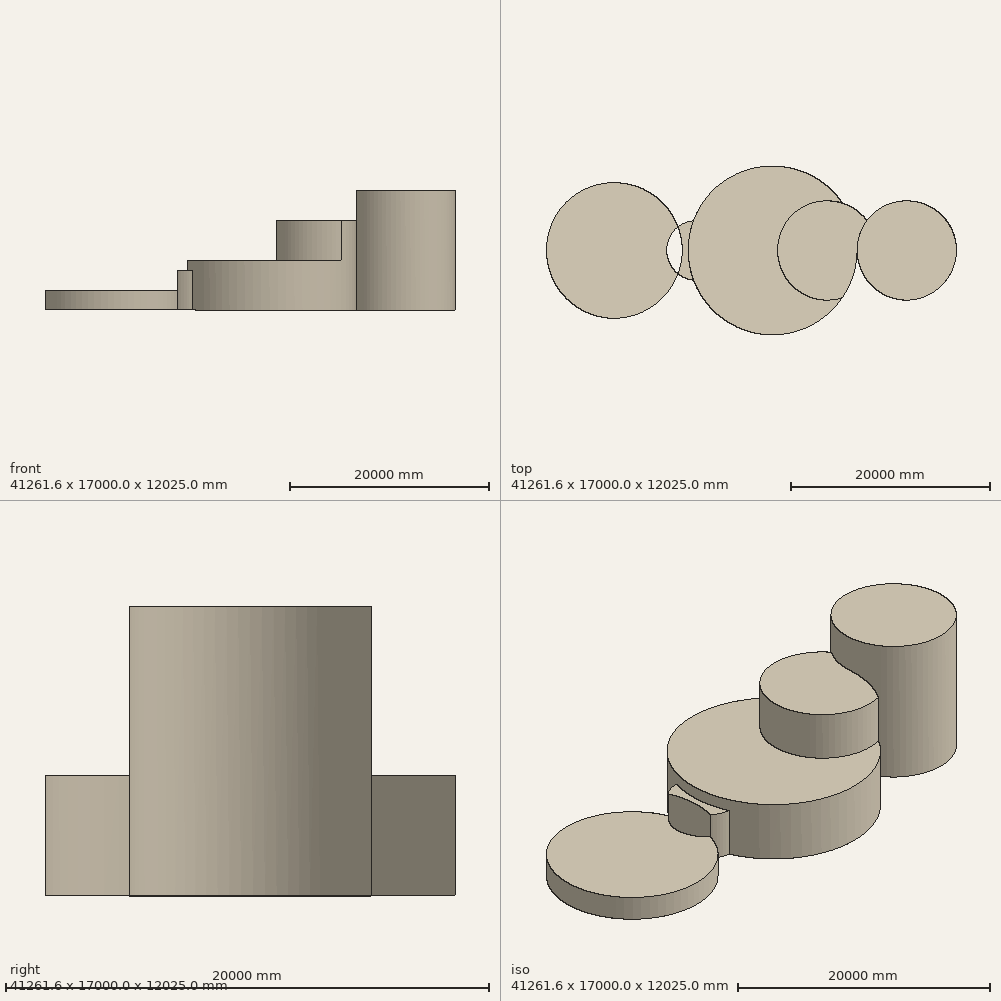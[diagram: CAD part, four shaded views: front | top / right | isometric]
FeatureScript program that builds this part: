
annotation { "Feature Type Name" : "Feature", "Feature Type Description" : "" }
export const myFeature = defineFeature(function(context is Context, id is Id, definition is map)
    precondition{}
    {
        {
            var Q0;
            Q0=qCreatedBy(makeId("Top.planeOp"),FACE);
            var sketch = newSketch(context, id + "F0", { "sketchPlane" : qUnion([Q0])});
            skCircle(sketch, "E0", {"center": v(0, 0) * mm, "radius": 5000 * mm});
            skCircle(sketch, "E1", {"center": v(-8000, 0) * mm, "radius": 5000 * mm});
            skCircle(sketch, "E2", {"center": v(-13500, 0) * mm, "radius": 8500 * mm});
            skCircle(sketch, "E3", {"center": v(-21161.23, 0) * mm, "radius": 3000 * mm});
            skCircle(sketch, "E4", {"center": v(-29430.74, 0) * mm, "radius": 6830.87 * mm});
            skSolve(sketch);
        }
        {
            var Q0;
            {var subQ0=sQuery(id+"F0.wireOp",EDGE,"E1");var subQ1=sQuery(id+"F0.wireOp",EDGE,"E0");var subQ2=makeQuery(id+"F0.imprint","INTERSECT",VERTEX,{"disambiguationData":[OD(0.0)],"derivedFrom":[subQ1,subQ0]});Q0=makeQuery(id+"F0.imprint","IMPRINT",FACE,{"disambiguationData":[TD([[makeQuery(id+"F0.imprint","IMPRINT",EDGE,{"disambiguationData":[TD([[subQ2,1.0]])],"derivedFrom":subQ1}),1.0]])]});}
            var Q1;
            {var subQ0=sQuery(id+"F0.wireOp",EDGE,"E1");var subQ1=sQuery(id+"F0.wireOp",EDGE,"E0");var subQ2=makeQuery(id+"F0.imprint","INTERSECT",VERTEX,{"disambiguationData":[OD(0.0)],"derivedFrom":[subQ1,subQ0]});Q1=makeQuery(id+"F0.imprint","IMPRINT",FACE,{"disambiguationData":[TD([[makeQuery(id+"F0.imprint","IMPRINT",EDGE,{"disambiguationData":[TD([[subQ2,-1.0]])],"derivedFrom":subQ1}),1.0]])]});}
            extrude(context, id + "F1", {"entities" : qUnion([Q0, Q1]), "depth" : 12000 * mm, "offsetDistance" : 25 * mm});
        }
        {
            var Q0;
            {var subQ0=sQuery(id+"F0.wireOp",EDGE,"E1");var subQ1=sQuery(id+"F0.wireOp",EDGE,"E0");var subQ2=makeQuery(id+"F0.imprint","INTERSECT",VERTEX,{"disambiguationData":[OD(0.0)],"derivedFrom":[subQ1,subQ0]});Q0=makeQuery(id+"F0.imprint","IMPRINT",FACE,{"disambiguationData":[TD([[makeQuery(id+"F0.imprint","IMPRINT",EDGE,{"disambiguationData":[TD([[subQ2,-1.0]])],"derivedFrom":subQ1}),-1.0]])]});}
            var Q1;
            {var subQ0=sQuery(id+"F0.wireOp",EDGE,"E2");var subQ1=sQuery(id+"F0.wireOp",EDGE,"E1");var subQ2=makeQuery(id+"F0.imprint","INTERSECT",VERTEX,{"disambiguationData":[OD(0.0)],"derivedFrom":[subQ1,subQ0]});Q1=makeQuery(id+"F0.imprint","IMPRINT",FACE,{"disambiguationData":[TD([[makeQuery(id+"F0.imprint","IMPRINT",EDGE,{"disambiguationData":[TD([[subQ2,-1.0]])],"derivedFrom":subQ1}),1.0]])]});}
            extrude(context, id + "F2", {"entities" : qUnion([Q0, Q1]), "operationType" : NewBodyOperationType.ADD, "depth" : 9000 * mm, "offsetDistance" : 25 * mm, "hasSecondDirection" : true, "secondDirectionOppositeDirection" : true, "secondDirectionDepth" : 25 * mm});
        }
        {
            var Q0;
            {var subQ0=sQuery(id+"F0.wireOp",EDGE,"E4");var subQ1=sQuery(id+"F0.wireOp",EDGE,"E2");var subQ2=makeQuery(id+"F0.imprint","INTERSECT",VERTEX,{"disambiguationData":[OD(0.0)],"derivedFrom":[subQ1,subQ0]});Q0=makeQuery(id+"F0.imprint","IMPRINT",FACE,{"disambiguationData":[TD([[makeQuery(id+"F0.imprint","IMPRINT",EDGE,{"disambiguationData":[TD([[subQ2,-1.0]])],"derivedFrom":subQ1}),1.0]])]});}
            var Q1;
            {var subQ0=sQuery(id+"F0.wireOp",EDGE,"E3");var subQ1=sQuery(id+"F0.wireOp",EDGE,"E2");var subQ2=makeQuery(id+"F0.imprint","INTERSECT",VERTEX,{"disambiguationData":[OD(0.0)],"derivedFrom":[subQ1,subQ0]});Q1=makeQuery(id+"F0.imprint","IMPRINT",FACE,{"disambiguationData":[TD([[makeQuery(id+"F0.imprint","IMPRINT",EDGE,{"disambiguationData":[TD([[subQ2,-1.0]])],"derivedFrom":subQ1}),1.0]])]});}
            var Q2;
            {var subQ0=sQuery(id+"F0.wireOp",EDGE,"E2");var subQ1=sQuery(id+"F0.wireOp",EDGE,"E1");var subQ2=makeQuery(id+"F0.imprint","INTERSECT",VERTEX,{"disambiguationData":[OD(0.0)],"derivedFrom":[subQ1,subQ0]});Q2=makeQuery(id+"F0.imprint","IMPRINT",FACE,{"disambiguationData":[TD([[makeQuery(id+"F0.imprint","IMPRINT",EDGE,{"disambiguationData":[TD([[subQ2,-1.0]])],"derivedFrom":subQ1}),-1.0]])]});}
            extrude(context, id + "F3", {"entities" : qUnion([Q0, Q1, Q2]), "operationType" : NewBodyOperationType.ADD, "depth" : 5000 * mm, "offsetDistance" : 25 * mm});
        }
        {
            var Q0;
            {var subQ0=sQuery(id+"F0.wireOp",EDGE,"E3");var subQ1=sQuery(id+"F0.wireOp",EDGE,"E2");var subQ2=makeQuery(id+"F0.imprint","INTERSECT",VERTEX,{"disambiguationData":[OD(0.0)],"derivedFrom":[subQ1,subQ0]});Q0=makeQuery(id+"F0.imprint","IMPRINT",FACE,{"disambiguationData":[TD([[makeQuery(id+"F0.imprint","IMPRINT",EDGE,{"disambiguationData":[TD([[subQ2,-1.0]])],"derivedFrom":subQ1}),-1.0]])]});}
            var Q1;
            {var subQ0=sQuery(id+"F0.wireOp",EDGE,"E3");var subQ1=sQuery(id+"F0.wireOp",EDGE,"E2");var subQ2=makeQuery(id+"F0.imprint","INTERSECT",VERTEX,{"disambiguationData":[OD(1.0)],"derivedFrom":[subQ1,subQ0]});Q1=makeQuery(id+"F0.imprint","IMPRINT",FACE,{"disambiguationData":[TD([[makeQuery(id+"F0.imprint","IMPRINT",EDGE,{"disambiguationData":[TD([[subQ2,1.0]])],"derivedFrom":subQ1}),-1.0]])]});}
            var Q2;
            {var subQ0=sQuery(id+"F0.wireOp",EDGE,"E4");var subQ1=sQuery(id+"F0.wireOp",EDGE,"E2");var subQ2=makeQuery(id+"F0.imprint","INTERSECT",VERTEX,{"disambiguationData":[OD(0.0)],"derivedFrom":[subQ1,subQ0]});Q2=makeQuery(id+"F0.imprint","IMPRINT",FACE,{"disambiguationData":[TD([[makeQuery(id+"F0.imprint","IMPRINT",EDGE,{"disambiguationData":[TD([[subQ2,-1.0]])],"derivedFrom":subQ1}),-1.0]])]});}
            extrude(context, id + "F4", {"entities" : qUnion([Q0, Q1, Q2]), "operationType" : NewBodyOperationType.ADD, "depth" : 4000 * mm, "offsetDistance" : 25 * mm});
        }
        {
            var Q0;
            {var subQ0=sQuery(id+"F0.wireOp",EDGE,"E4");var subQ1=sQuery(id+"F0.wireOp",EDGE,"E3");var subQ2=makeQuery(id+"F0.imprint","INTERSECT",VERTEX,{"disambiguationData":[OD(0.0)],"derivedFrom":[subQ1,subQ0]});Q0=makeQuery(id+"F0.imprint","IMPRINT",FACE,{"disambiguationData":[TD([[makeQuery(id+"F0.imprint","IMPRINT",EDGE,{"disambiguationData":[TD([[subQ2,-1.0]])],"derivedFrom":subQ1}),-1.0]])]});}
            extrude(context, id + "F5", {"entities" : qUnion([Q0]), "operationType" : NewBodyOperationType.ADD, "depth" : 2000 * mm, "offsetDistance" : 25 * mm});
        }
    });
